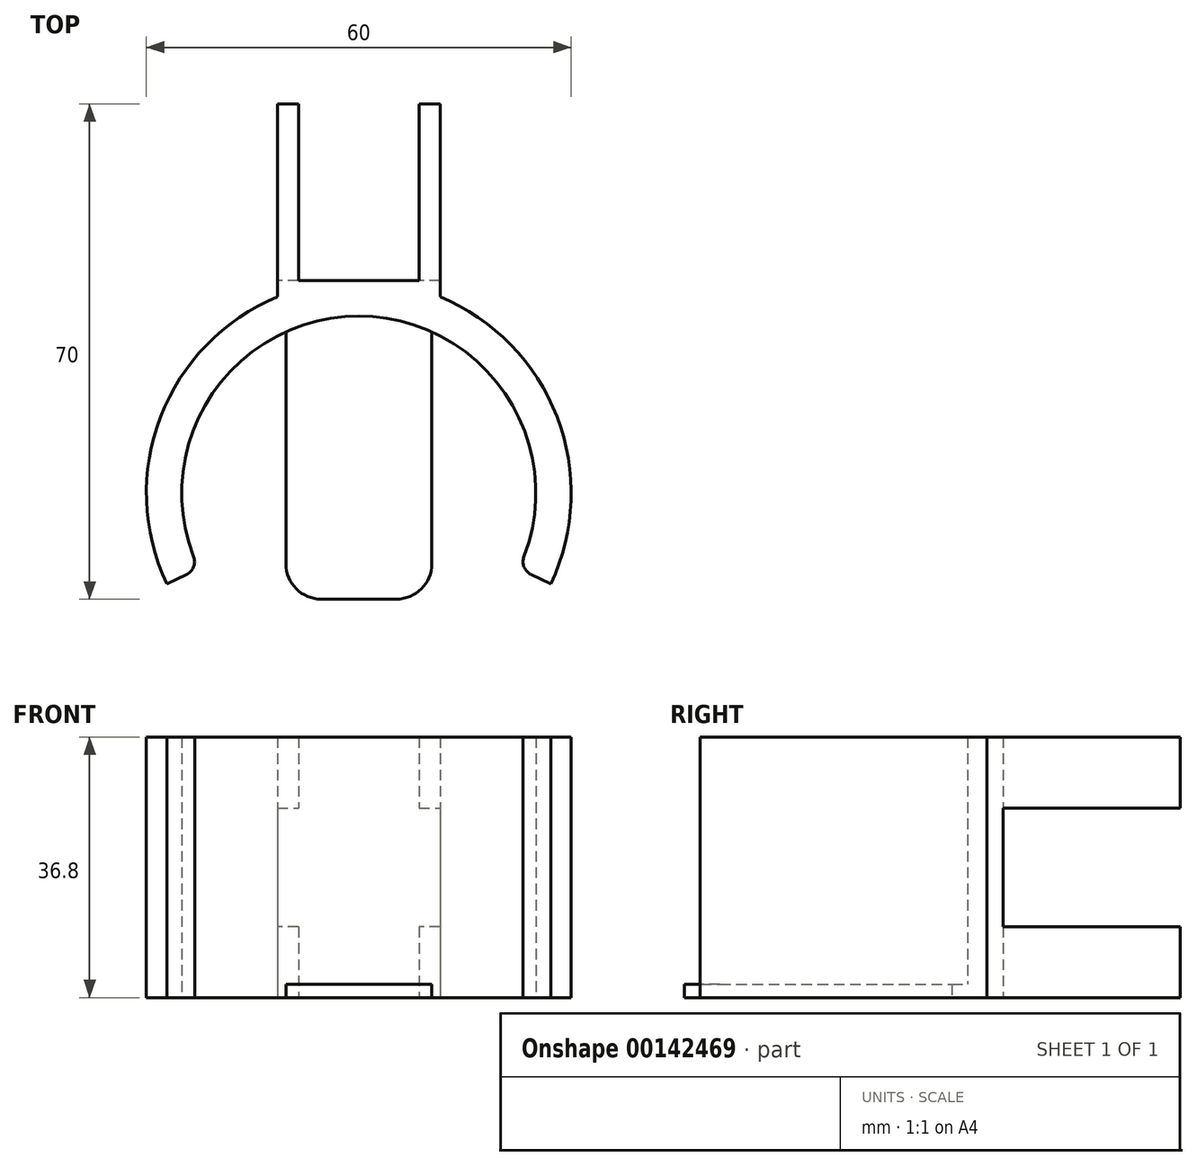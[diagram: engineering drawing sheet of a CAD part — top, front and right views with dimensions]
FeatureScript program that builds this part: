
annotation { "Feature Type Name" : "Feature", "Feature Type Description" : "" }
export const myFeature = defineFeature(function(context is Context, id is Id, definition is map)
    precondition{}
    {
        {
            var Q0;
            Q0=qCreatedBy(makeId("Top.planeOp"),FACE);
            var sketch = newSketch(context, id + "F0", { "sketchPlane" : qUnion([Q0])});
            skLineSegment(sketch, "E0", {"start": v(0, 0) * mm, "end": v(-11.5, 0) * mm});
            skLineSegment(sketch, "E1", {"start": v(-11.5, 0) * mm, "end": v(-11.5, 30) * mm});
            skLineSegment(sketch, "E2", {"start": v(-11.5, 30) * mm, "end": v(-8.5, 30) * mm});
            skLineSegment(sketch, "E3", {"start": v(-8.5, 30) * mm, "end": v(-8.5, 5) * mm});
            skLineSegment(sketch, "E4", {"start": v(-8.5, 5) * mm, "end": v(0, 5) * mm});
            skLineSegment(sketch, "E5.MirrorCS", {"start": v(0, 0) * mm, "end": v(11.5, 0) * mm});
            skLineSegment(sketch, "E6.MirrorCS", {"start": v(11.5, 30) * mm, "end": v(8.5, 30) * mm});
            skLineSegment(sketch, "E7.MirrorCS", {"start": v(8.5, 5) * mm, "end": v(0, 5) * mm});
            skLineSegment(sketch, "E8.MirrorCS", {"start": v(11.5, 0) * mm, "end": v(11.5, 30) * mm});
            skLineSegment(sketch, "E9.MirrorCS", {"start": v(8.5, 30) * mm, "end": v(8.5, 5) * mm});
            skSolve(sketch);
        }
        {
            var Q0;
            Q0 = qSketchRegion(id + "F0", true);
            extrude(context, id + "F1", {"entities" : qUnion([Q0]), "depth" : 10 * mm});
        }
        {
            var Q0;
            Q0=makeQuery(id+"F1.opExtrude","CAP_FACE",FACE,{"disambiguationData":[OSD([sQuery(id+"F0.wireOp",EDGE,"E0"),sQuery(id+"F0.wireOp",EDGE,"E1"),sQuery(id+"F0.wireOp",EDGE,"E2"),sQuery(id+"F0.wireOp",EDGE,"E3"),sQuery(id+"F0.wireOp",EDGE,"E4"),sQuery(id+"F0.wireOp",EDGE,"E5.MirrorCS"),sQuery(id+"F0.wireOp",EDGE,"E6.MirrorCS"),sQuery(id+"F0.wireOp",EDGE,"E7.MirrorCS"),sQuery(id+"F0.wireOp",EDGE,"E8.MirrorCS"),sQuery(id+"F0.wireOp",EDGE,"E9.MirrorCS")])],"isStart":false});
            var sketch = newSketch(context, id + "F2", { "sketchPlane" : qUnion([Q0])});
            skLineSegment(sketch, "E10.bottom", {"start": v(-11.5, 0) * mm, "end": v(11.5, 0) * mm});
            skLineSegment(sketch, "E10.top", {"start": v(-11.5, 5) * mm, "end": v(11.5, 5) * mm});
            skLineSegment(sketch, "E10.left", {"start": v(-11.5, 0) * mm, "end": v(-11.5, 5) * mm});
            skLineSegment(sketch, "E10.right", {"start": v(11.5, 0) * mm, "end": v(11.5, 5) * mm});
            skArc(sketch, "E11", {"start": v(22.6, -35.69) * mm, "mid": v(0, 0) * mm, "end": v(-22.6, -35.69) * mm});
            skArc(sketch, "E12", {"start": v(27.12, -37.82) * mm, "mid": v(0, 5) * mm, "end": v(-27.12, -37.82) * mm});
            skLineSegment(sketch, "E13", {"start": v(0, -25) * mm, "end": v(-27.12, -37.82) * mm});
            skLineSegment(sketch, "E14.MirrorCS", {"start": v(0, -25) * mm, "end": v(27.12, -37.82) * mm});
            skSolve(sketch);
        }
        {
            var Q0;
            {var subQ3=sQuery(id+"F2.wireOp",EDGE,"E10.left");var subQ7=sQuery(id+"F2.wireOp",EDGE,"E10.bottom");var subQ8=makeQuery(id+"F2.imprint","INTERSECT",VERTEX,{"derivedFrom":[subQ7,subQ3]});Q0=makeQuery(id+"F2.imprint","IMPRINT",FACE,{"disambiguationData":[TD([[makeQuery(id+"F2.imprint","IMPRINT",EDGE,{"disambiguationData":[TD([[subQ8,1.0]])],"derivedFrom":subQ7}),1.0]])]});}
            var Q1;
            {var subQ3=sQuery(id+"F2.wireOp",EDGE,"E10.right");var subQ7=sQuery(id+"F2.wireOp",EDGE,"E10.bottom");var subQ9=makeQuery(id+"F2.imprint","INTERSECT",VERTEX,{"derivedFrom":[subQ7,subQ3]});Q1=makeQuery(id+"F2.imprint","IMPRINT",FACE,{"disambiguationData":[TD([[makeQuery(id+"F2.imprint","IMPRINT",EDGE,{"disambiguationData":[TD([[subQ9,-1.0]])],"derivedFrom":subQ7}),1.0]])]});}
            var Q2;
            {var subQ1=sQuery(id+"F2.wireOp",EDGE,"E10.bottom");var subQ6=sQuery(id+"F2.wireOp",EDGE,"E10.right");var subQ8=makeQuery(id+"F2.imprint","INTERSECT",VERTEX,{"derivedFrom":[subQ1,subQ6]});Q2=makeQuery(id+"F2.imprint","IMPRINT",FACE,{"disambiguationData":[TD([[makeQuery(id+"F2.imprint","IMPRINT",EDGE,{"disambiguationData":[TD([[subQ8,-1.0]])],"derivedFrom":subQ1}),-1.0]])]});}
            var Q3;
            {var subQ0=sQuery(id+"F2.wireOp",EDGE,"E10.top");var subQ4=sQuery(id+"F2.wireOp",EDGE,"E12");var subQ5=makeQuery(id+"F2.imprint","INTERSECT",VERTEX,{"derivedFrom":[subQ0,subQ4]});Q3=makeQuery(id+"F2.imprint","IMPRINT",FACE,{"disambiguationData":[TD([[makeQuery(id+"F2.imprint","IMPRINT",EDGE,{"disambiguationData":[TD([[subQ5,-1.0]])],"derivedFrom":subQ0}),1.0]])]});}
            var Q4;
            {var subQ0=sQuery(id+"F2.wireOp",EDGE,"E10.top");var subQ2=sQuery(id+"F2.wireOp",EDGE,"E12");var subQ3=makeQuery(id+"F2.imprint","INTERSECT",VERTEX,{"derivedFrom":[subQ0,subQ2]});Q4=makeQuery(id+"F2.imprint","IMPRINT",FACE,{"disambiguationData":[TD([[makeQuery(id+"F2.imprint","IMPRINT",EDGE,{"disambiguationData":[TD([[subQ3,1.0]])],"derivedFrom":subQ0}),1.0]])]});}
            var Q5;
            Q5=makeQuery(id+"F1.opExtrude","CAP_FACE",FACE,{"disambiguationData":[OSD([sQuery(id+"F0.wireOp",EDGE,"E0"),sQuery(id+"F0.wireOp",EDGE,"E1"),sQuery(id+"F0.wireOp",EDGE,"E2"),sQuery(id+"F0.wireOp",EDGE,"E3"),sQuery(id+"F0.wireOp",EDGE,"E4"),sQuery(id+"F0.wireOp",EDGE,"E5.MirrorCS"),sQuery(id+"F0.wireOp",EDGE,"E6.MirrorCS"),sQuery(id+"F0.wireOp",EDGE,"E7.MirrorCS"),sQuery(id+"F0.wireOp",EDGE,"E8.MirrorCS"),sQuery(id+"F0.wireOp",EDGE,"E9.MirrorCS")])],"isStart":true});
            extrude(context, id + "F3", {"entities" : qUnion([Q0, Q1, Q2, Q3, Q4]), "operationType" : NewBodyOperationType.ADD, "depth" : 16.8 * mm, "hasSecondDirection" : true, "secondDirectionBound" : SecondDirectionBoundingType.UP_TO_SURFACE, "secondDirectionOppositeDirection" : true, "secondDirectionBoundEntityFace" : qUnion([Q5]), "secondDirectionDepth" : 25 * mm});
        }
        {
            var Q0;
            Q0=makeQuery(id+"F3.opExtrude","CAP_FACE",FACE,{"disambiguationData":[OSD([sQuery(id+"F2.wireOp",EDGE,"E10.bottom"),sQuery(id+"F2.wireOp",EDGE,"E10.top"),sQuery(id+"F2.wireOp",EDGE,"E10.left"),sQuery(id+"F2.wireOp",EDGE,"E10.right")])],"isStart":false});
            var sketch = newSketch(context, id + "F4", { "sketchPlane" : qUnion([Q0])});
            skLineSegment(sketch, "E15", {"start": v(0, 0) * mm, "end": v(-11.5, 0) * mm});
            skLineSegment(sketch, "E16", {"start": v(-11.5, 0) * mm, "end": v(-11.5, 30) * mm});
            skLineSegment(sketch, "E17", {"start": v(-11.5, 30) * mm, "end": v(-8.5, 30) * mm});
            skLineSegment(sketch, "E18", {"start": v(-8.5, 30) * mm, "end": v(-8.5, 5) * mm});
            skLineSegment(sketch, "E19", {"start": v(-8.5, 5) * mm, "end": v(0, 5) * mm});
            skLineSegment(sketch, "E20.MirrorCS", {"start": v(8.5, 30) * mm, "end": v(8.5, 5) * mm});
            skLineSegment(sketch, "E21.MirrorCS", {"start": v(8.5, 5) * mm, "end": v(0, 5) * mm});
            skLineSegment(sketch, "E22.MirrorCS", {"start": v(11.5, 30) * mm, "end": v(8.5, 30) * mm});
            skLineSegment(sketch, "E23.MirrorCS", {"start": v(0, 0) * mm, "end": v(11.5, 0) * mm});
            skLineSegment(sketch, "E24.MirrorCS", {"start": v(11.5, 0) * mm, "end": v(11.5, 30) * mm});
            skSolve(sketch);
        }
        {
            var Q0;
            Q0 = qSketchRegion(id + "F4", true);
            extrude(context, id + "F5", {"entities" : qUnion([Q0]), "operationType" : NewBodyOperationType.ADD, "depth" : 10 * mm});
        }
        {
            var Q0;
            {var subQ0=sQuery(id+"F2.wireOp",EDGE,"E11");var subQ1=sQuery(id+"F2.wireOp",EDGE,"E10.left");var subQ2=sQuery(id+"F2.wireOp",EDGE,"E13");var subQ3=sQuery(id+"F2.wireOp",EDGE,"E12");var subQ4=makeQuery(id+"F3.opExtrude","CAP_FACE",FACE,{"disambiguationData":[OSD([sQuery(id+"F2.wireOp",EDGE,"E10.top"),subQ1,sQuery(id+"F2.wireOp",EDGE,"E10.right"),subQ0,subQ3,subQ2,sQuery(id+"F2.wireOp",EDGE,"E14.MirrorCS")])],"isStart":false});Q0=makeQuery(id+"F5.boolean.opBoolean","SPLIT",FACE,{"disambiguationData":[TD([makeQuery(id+"F1.opExtrude","SWEPT_FACE",FACE,{"disambiguationData":[OSD([sQuery(id+"F0.wireOp",EDGE,"E1")])]})])],"derivedFrom":subQ4});}
            var Q1;
            {var subQ0=sQuery(id+"F2.wireOp",EDGE,"E11");var subQ1=sQuery(id+"F2.wireOp",EDGE,"E10.right");var subQ2=sQuery(id+"F2.wireOp",EDGE,"E14.MirrorCS");var subQ3=sQuery(id+"F2.wireOp",EDGE,"E12");var subQ4=makeQuery(id+"F3.opExtrude","CAP_FACE",FACE,{"disambiguationData":[OSD([sQuery(id+"F2.wireOp",EDGE,"E10.top"),sQuery(id+"F2.wireOp",EDGE,"E10.left"),subQ1,subQ0,subQ3,sQuery(id+"F2.wireOp",EDGE,"E13"),subQ2])],"isStart":false});Q1=makeQuery(id+"F5.boolean.opBoolean","SPLIT",FACE,{"disambiguationData":[TD([makeQuery(id+"F1.opExtrude","SWEPT_FACE",FACE,{"disambiguationData":[OSD([sQuery(id+"F0.wireOp",EDGE,"E8.MirrorCS")])]})])],"derivedFrom":subQ4});}
            var Q2;
            Q2=makeQuery(id+"F5.opExtrude","CAP_FACE",FACE,{"disambiguationData":[OSD([sQuery(id+"F4.wireOp",EDGE,"E15"),sQuery(id+"F4.wireOp",EDGE,"E16"),sQuery(id+"F4.wireOp",EDGE,"E17"),sQuery(id+"F4.wireOp",EDGE,"E18"),sQuery(id+"F4.wireOp",EDGE,"E19"),sQuery(id+"F4.wireOp",EDGE,"E20.MirrorCS"),sQuery(id+"F4.wireOp",EDGE,"E21.MirrorCS"),sQuery(id+"F4.wireOp",EDGE,"E22.MirrorCS"),sQuery(id+"F4.wireOp",EDGE,"E23.MirrorCS"),sQuery(id+"F4.wireOp",EDGE,"E24.MirrorCS")])],"isStart":false});
            extrude(context, id + "F6", {"entities" : qUnion([Q0, Q1]), "operationType" : NewBodyOperationType.ADD, "endBound" : BoundingType.UP_TO_SURFACE, "endBoundEntityFace" : qUnion([Q2]), "depth" : 10 * mm});
        }
        {
            var Q0;
            {var subQ0=sQuery(id+"F2.wireOp",EDGE,"E14.MirrorCS");var subQ1=sQuery(id+"F2.wireOp",EDGE,"E11");Q0=makeQuery(id+"F6.boolean.opBoolean","MERGE",EDGE,{"derivedFrom":[makeQuery(id+"F3.opExtrude","SWEPT_EDGE",EDGE,{"disambiguationData":[OSD([subQ1,subQ0])]}),makeQuery(id+"F6.opExtrude","SWEPT_EDGE",EDGE,{"disambiguationData":[OSD([subQ1,subQ0])]})]});}
            var Q1;
            {var subQ0=sQuery(id+"F2.wireOp",EDGE,"E13");var subQ1=sQuery(id+"F2.wireOp",EDGE,"E11");Q1=makeQuery(id+"F6.boolean.opBoolean","MERGE",EDGE,{"derivedFrom":[makeQuery(id+"F3.opExtrude","SWEPT_EDGE",EDGE,{"disambiguationData":[OSD([subQ1,subQ0])]}),makeQuery(id+"F6.opExtrude","SWEPT_EDGE",EDGE,{"disambiguationData":[OSD([subQ1,subQ0])]})]});}
            fillet(context, id + "F7", {"entities" : qUnion([Q0, Q1]), "radius" : 2 * mm, "tangentPropagation" : true, "allowEdgeOverflow" : false});
        }
        {
            var Q0;
            Q0=qCreatedBy(makeId("Front.planeOp"),FACE);
            var sketch = newSketch(context, id + "F8", { "sketchPlane" : qUnion([Q0])});
            skLineSegment(sketch, "E25", {"start": v(0, 0) * mm, "end": v(-10.3, 0) * mm});
            skLineSegment(sketch, "E26", {"start": v(-10.3, 0) * mm, "end": v(-10.3, 1.86) * mm});
            skLineSegment(sketch, "E27", {"start": v(-10.3, 1.86) * mm, "end": v(0, 1.86) * mm});
            skLineSegment(sketch, "E28.MirrorCS", {"start": v(10.3, 1.86) * mm, "end": v(0, 1.86) * mm});
            skLineSegment(sketch, "E29.MirrorCS", {"start": v(10.3, 0) * mm, "end": v(10.3, 1.86) * mm});
            skLineSegment(sketch, "E30.MirrorCS", {"start": v(0, 0) * mm, "end": v(10.3, 0) * mm});
            skSolve(sketch);
        }
        {
            var Q0;
            Q0 = qSketchRegion(id + "F8", true);
            extrude(context, id + "F9", {"entities" : qUnion([Q0]), "operationType" : NewBodyOperationType.ADD, "depth" : 40 * mm});
        }
        {
            var Q0;
            Q0=makeQuery(id+"F9.opExtrude","CAP_EDGE",EDGE,{"disambiguationData":[OSD([sQuery(id+"F8.wireOp",EDGE,"E26")])],"isStart":false});
            var Q1;
            Q1=makeQuery(id+"F9.opExtrude","CAP_EDGE",EDGE,{"disambiguationData":[OSD([sQuery(id+"F8.wireOp",EDGE,"E29.MirrorCS")])],"isStart":false});
            fillet(context, id + "F10", {"entities" : qUnion([Q0, Q1]), "radius" : 5 * mm, "tangentPropagation" : true, "allowEdgeOverflow" : false});
        }
    });
